# Revit family: Access Restriction Device
name_source: partatom
category: Generic Models
units: mm (PartAtom-declared; Revit-internal decimal feet)

## family parameters
Always vertical = Yes
Can host rebar = No
Cut with Voids When Loaded = No
Maintain Annotation Orientation = No
Part Type = Normal
Room Calculation Point = No
Round Connector Dimension = Use Diameter
Shared = No
Work Plane-Based = No

## types (1)
- Access Restriction Device
    Combined Balustrade Decking Width = 0 mm  [stored 0 ft]
    Default Elevation = 0 mm  [stored 0 ft]
    Height = 1200 mm
    Thickness = 100 mm  [stored 0.328084 ft]
    Vertical distance between Handrail and Device = 0 mm  [stored 0 ft]
    Width = 500 mm  [stored 1.64042 ft]
    Width of Lower Outer Decking = 0 mm  [stored 0 ft]

note: [stored X ft] marks values corroborated as IEEE doubles in the binary element streams (Revit-internal decimal feet)

## geometry (parser evidence)
native form markers: Sweep x3
no freeform markers — native parametric forms only
